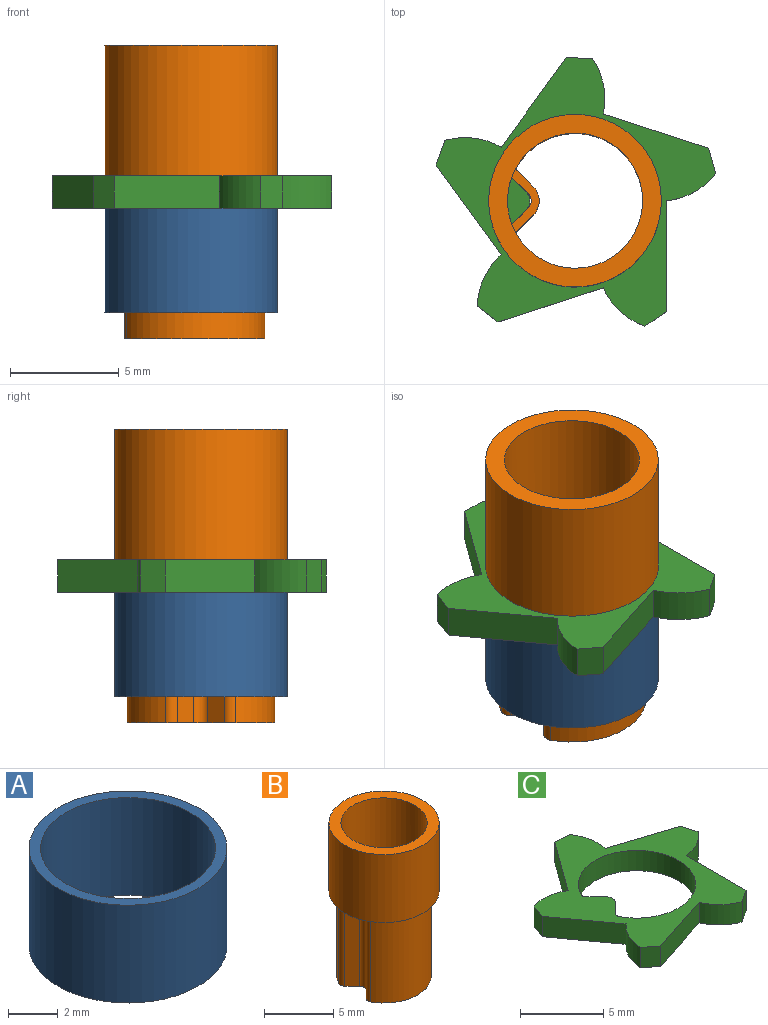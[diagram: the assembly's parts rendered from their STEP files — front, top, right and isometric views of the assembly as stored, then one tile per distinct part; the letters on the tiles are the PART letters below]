
ASSEMBLY  parts=3 mates=2
PART A: 4 faces, bbox 7.9x7.9x4.8 mm
  f0: cylinder r=3.51mm len=7.02mm, axis (0,0,-1), area 105.8mm2, adj f2,f3
  f1: cylinder r=3.97mm len=7.94mm, axis (0,0,-1), area 119.7mm2, adj f2,f3
  f2: plane 7.94x7.94mm, normal (0,0,1), area 10.8mm2, adj f0,f1
  f3: plane 7.94x7.94mm, normal (0,0,-1), area 10.8mm2, adj f0,f1
PART B: 17 faces, bbox 7.9x7.9x13.5 mm
  f0: cylinder r=3.11mm len=13.5mm, axis (0,0,-1), area 239mm2, adj f2,f3,f4,f14,f15,f16
  f1: cylinder r=3.97mm len=7.94mm, axis (0,0,-1), area 149.7mm2, adj f2,f3
  f2: plane 7.94x7.94mm, normal (0,0,1), area 19.2mm2, adj f0,f1
  f3: plane 7.94x7.94mm, normal (0,0,-1), area 14mm2, adj f0,f1,f9,f10,f11
  f4: cylinder r=0.15mm len=7.5mm, axis (0,0,1), area 1.5mm2, adj f0,f5,f15,f16
  f5: plane 7.5x0.75mm, normal (0.71,0.71,0), area 7.9mm2, adj f4,f6,f15,f16
  f6: cylinder r=0.9mm len=7.5mm, axis (0,0,1), area 10.6mm2, adj f5,f7,f15,f16
  f7: plane 7.5x0.75mm, normal (0.71,-0.71,0), area 7.9mm2, adj f6,f14,f15,f16
  f8: plane 7.5x0.76mm, normal (-0.71,-0.71,0), area 8.1mm2, adj f9,f13,f15,f16
  f9: cylinder r=0.45mm len=7.5mm, axis (0,0,1), area 4.3mm2, adj f3,f8,f10,f15,f16
  f10: cylinder r=3.4mm len=7.5mm, axis (0,0,1), area 134.8mm2, adj f3,f9,f11,f15
  f11: cylinder r=0.45mm len=7.5mm, axis (0,0,1), area 4.3mm2, adj f3,f10,f12,f15,f16
  f12: plane 7.5x0.76mm, normal (-0.71,0.71,0), area 8.1mm2, adj f11,f13,f15,f16
  f13: cylinder r=0.45mm len=7.5mm, axis (0,0,1), area 5.3mm2, adj f8,f12,f15,f16
  f14: cylinder r=0.15mm len=7.5mm, axis (0,0,1), area 1.5mm2, adj f0,f7,f15,f16
  f15: plane 6.79x6.44mm, normal (0,0,-1), area 6.4mm2, adj f0,f4,f5,f6,f7,f8,f9,f10
  f16: plane 3.13x1.26mm, normal (0,0,1), area 1.3mm2, adj f0,f4,f5,f6,f7,f8,f9,f11
PART C: 23 faces, bbox 12.9x12.4x1.5 mm
  f0: plane 5.09x1.5mm, normal (1,0,0), area 7.6mm2, adj f1,f20,f21,f22
  f1: cylinder r=3.29mm len=2.28mm, axis (0,0,-1), area 4mm2, adj f0,f2,f21,f22
  f2: plane 1.5x1.15mm, normal (0.96,0.28,0), area 1.8mm2, adj f1,f3,f21,f22
  f3: plane 4.84x1.57mm, normal (0.31,0.95,0), area 7.6mm2, adj f2,f4,f21,f22
  f4: cylinder r=3.29mm len=2.56mm, axis (0,0,-1), area 4mm2, adj f3,f5,f21,f22
  f5: plane 1.5x1.2mm, normal (0.03,1,0), area 1.8mm2, adj f4,f6,f21,f22
  f6: plane 4.12x2.99mm, normal (-0.81,0.59,0), area 7.6mm2, adj f5,f7,f21,f22
  f7: cylinder r=3.29mm len=2.59mm, axis (0,0,-1), area 4mm2, adj f6,f8,f21,f22
  f8: plane 1.5x1.13mm, normal (-0.94,0.34,0), area 1.8mm2, adj f7,f9,f21,f22
  f9: plane 4.12x2.99mm, normal (-0.81,-0.59,0), area 7.6mm2, adj f8,f10,f21,f22
  f10: cylinder r=3.29mm len=2.37mm, axis (0,0,-1), area 4mm2, adj f9,f11,f21,f22
  f11: plane 1.5x0.95mm, normal (-0.61,-0.79,0), area 1.8mm2, adj f10,f12,f21,f22
  f12: plane 4.84x1.57mm, normal (0.31,-0.95,0), area 7.6mm2, adj f11,f13,f21,f22
  f13: cylinder r=3.29mm len=1.91mm, axis (0,0,-1), area 4mm2, adj f12,f20,f21,f22
  f14: cylinder r=3.53mm len=7.06mm, axis (0,0,-1), area 28.3mm2, adj f15,f19,f21,f22
  f15: cylinder r=0.3mm len=1.5mm, axis (0,0,-1), area 0.6mm2, adj f14,f16,f21,f22
  f16: plane 1.5x0.83mm, normal (0.71,-0.71,0), area 1.8mm2, adj f15,f17,f21,f22
  f17: cylinder r=0.6mm len=1.5mm, axis (0,0,-1), area 1.4mm2, adj f16,f18,f21,f22
  f18: plane 1.5x0.83mm, normal (0.71,0.71,0), area 1.8mm2, adj f17,f19,f21,f22
  f19: cylinder r=0.3mm len=1.5mm, axis (0,0,-1), area 0.6mm2, adj f14,f18,f21,f22
  f20: plane 1.5x0.99mm, normal (0.56,-0.83,0), area 1.8mm2, adj f0,f13,f21,f22
  f21: plane 12.87x12.36mm, normal (0,0,1), area 52.2mm2, adj f0,f1,f2,f3,f4,f5,f6,f7
  f22: plane 12.87x12.36mm, normal (0,0,-1), area 52.2mm2, adj f0,f1,f2,f3,f4,f5,f6,f7
PLACE A t=(0,0,-5.3)mm
PLACE B t=(0,0,1)mm
PLACE C t=(0,0,-0.5)mm
MATE fastened C.f14 <-> A.f0  axis (0,0,-1) through (0,0,-0.5)mm
MATE fastened B.f0 <-> C.f14  axis (0,0,1) through (0,0,1)mm
